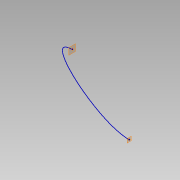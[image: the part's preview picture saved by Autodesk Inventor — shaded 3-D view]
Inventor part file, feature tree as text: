
AUTODESK INVENTOR PART (.ipt)
format: ipt  version: 2019 (Build 230136000, 136)  size: 88,064 bytes
history: native  units: mm
features: other x2, plane x2, sketch x1
ambient origin geometry x8: Origin, YZ Plane, XZ Plane, XY Plane, X Axis, Y Axis, Z Axis, Center Point
feature tree (5):
  other  "Punto de trabajo1"
  other  "Punto de trabajo2"
  plane  "Plano de trabajo1"
  plane  "Plano de trabajo2"
  sketch  "Boceto 3D1"  dims[d0=-10.0mm d1=-0.1mm d2=10.0mm d3=-0.1mm]
